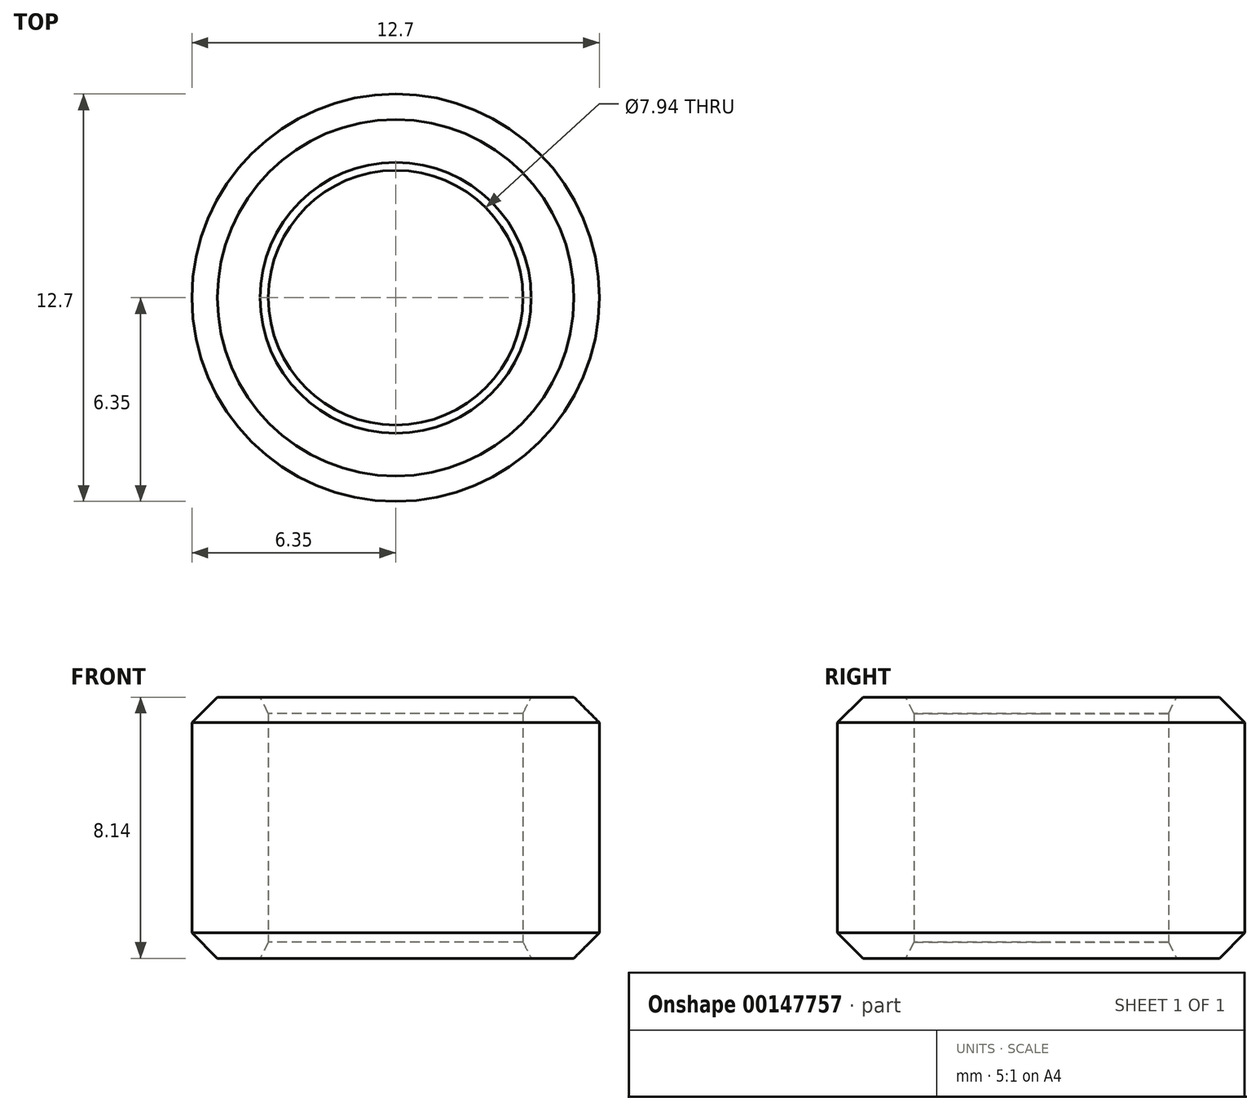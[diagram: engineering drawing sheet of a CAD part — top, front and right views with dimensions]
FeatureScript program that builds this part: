
annotation { "Feature Type Name" : "Feature", "Feature Type Description" : "" }
export const myFeature = defineFeature(function(context is Context, id is Id, definition is map)
    precondition{}
    {
        {
            var Q0;
            Q0=qCreatedBy(makeId("Top.planeOp"),FACE);
            var sketch = newSketch(context, id + "F0", { "sketchPlane" : qUnion([Q0])});
            skCircle(sketch, "E0", {"center": v(0, 0) * mm, "radius": 3.97 * mm});
            skCircle(sketch, "E1", {"center": v(0, 0) * mm, "radius": 6.35 * mm});
            skSolve(sketch);
        }
        {
            var Q0;
            Q0=makeQuery(id+"F0.imprint","IMPRINT",FACE,{"disambiguationData":[TD([[makeQuery(id+"F0.imprint","IMPRINT",EDGE,{"derivedFrom":sQuery(id+"F0.wireOp",EDGE,"E0")}),-1.0]])]});
            extrude(context, id + "F1", {"entities" : qUnion([Q0]), "depth" : 8.14 * mm});
        }
        {
            var Q0;
            Q0=makeQuery(id+"F1.opExtrude","CAP_EDGE",EDGE,{"disambiguationData":[OSD([sQuery(id+"F0.wireOp",EDGE,"E1")])],"isStart":false});
            var Q1;
            Q1=makeQuery(id+"F1.opExtrude","CAP_EDGE",EDGE,{"disambiguationData":[OSD([sQuery(id+"F0.wireOp",EDGE,"E1")])],"isStart":true});
            chamfer(context, id + "F2", {"entities" : qUnion([Q0, Q1]), "width" : 0.8 * mm, "tangentPropagation" : true});
        }
        {
            var Q0;
            Q0=makeQuery(id+"F1.opExtrude","CAP_EDGE",EDGE,{"disambiguationData":[OSD([sQuery(id+"F0.wireOp",EDGE,"E0")])],"isStart":false});
            var Q1;
            Q1=makeQuery(id+"F1.opExtrude","CAP_EDGE",EDGE,{"disambiguationData":[OSD([sQuery(id+"F0.wireOp",EDGE,"E0")])],"isStart":true});
            chamfer(context, id + "F3", {"entities" : qUnion([Q0, Q1]), "chamferType" : ChamferType.TWO_OFFSETS, "width1" : 0.5 * mm, "oppositeDirection" : false, "width2" : 0.25 * mm, "tangentPropagation" : true});
        }
    });
